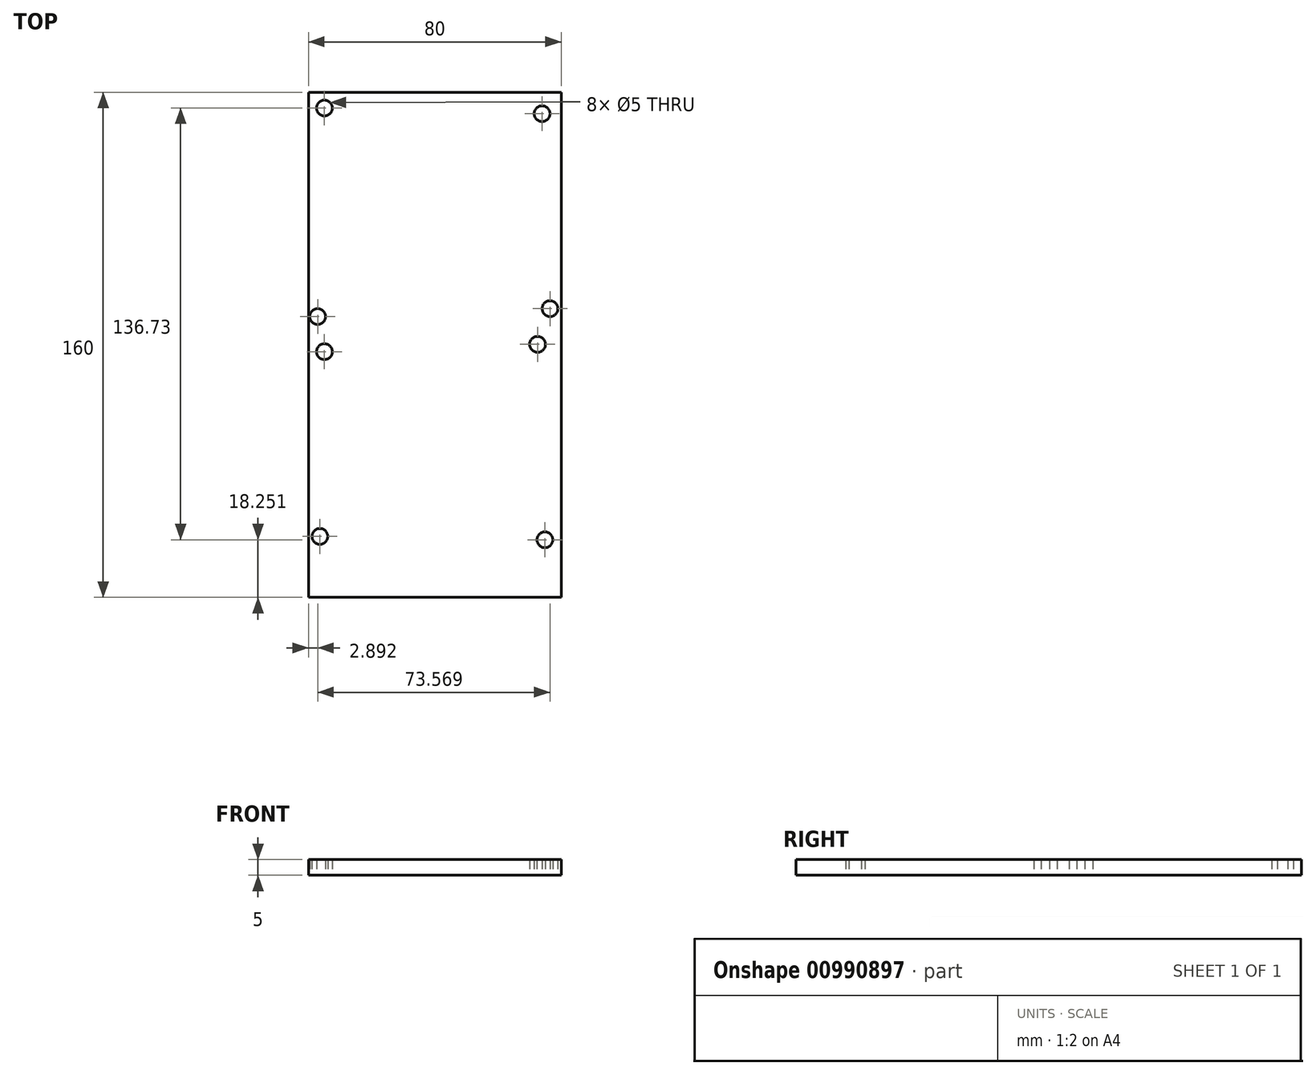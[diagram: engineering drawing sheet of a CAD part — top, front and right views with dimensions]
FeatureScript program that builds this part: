
annotation { "Feature Type Name" : "Feature", "Feature Type Description" : "" }
export const myFeature = defineFeature(function(context is Context, id is Id, definition is map)
    precondition{}
    {
        {
            var Q0;
            Q0=qCreatedBy(makeId("Top.planeOp"),FACE);
            var sketch = newSketch(context, id + "F0", { "sketchPlane" : qUnion([Q0])});
            skLineSegment(sketch, "E0.bottom", {"start": v(40, -80) * mm, "end": v(-40, -80) * mm});
            skLineSegment(sketch, "E0.top", {"start": v(40, 80) * mm, "end": v(-40, 80) * mm});
            skLineSegment(sketch, "E0.left", {"start": v(40, -80) * mm, "end": v(40, 80) * mm});
            skLineSegment(sketch, "E0.right", {"start": v(-40, -80) * mm, "end": v(-40, 80) * mm});
            skPoint(sketch, "E0.middle", {"position": v(0, 0) * mm});
            skLineSegment(sketch, "E1.bottom", {"start": v(30, -70) * mm, "end": v(-30, -70) * mm, "construction": true});
            skLineSegment(sketch, "E1.top", {"start": v(30, 70) * mm, "end": v(-30, 70) * mm, "construction": true});
            skLineSegment(sketch, "E1.left", {"start": v(30, -70) * mm, "end": v(30, 70) * mm, "construction": true});
            skLineSegment(sketch, "E1.right", {"start": v(-30, -70) * mm, "end": v(-30, 70) * mm, "construction": true});
            skCircle(sketch, "E2", {"center": v(-34.96, 74.98) * mm, "radius": 2.5 * mm});
            skCircle(sketch, "E3", {"center": v(140.96, 180.79) * mm, "radius": 2.5 * mm});
            skCircle(sketch, "E4", {"center": v(33.95, 73.2) * mm, "radius": 2.5 * mm});
            skCircle(sketch, "E5", {"center": v(36.46, 11.46) * mm, "radius": 2.5 * mm});
            skCircle(sketch, "E6", {"center": v(32.51, 0.16) * mm, "radius": 2.5 * mm});
            skCircle(sketch, "E7", {"center": v(-37.1, 8.95) * mm, "radius": 2.5 * mm});
            skCircle(sketch, "E8", {"center": v(-34.96, -2.18) * mm, "radius": 2.5 * mm});
            skCircle(sketch, "E9", {"center": v(-36.4, -60.67) * mm, "radius": 2.5 * mm});
            skCircle(sketch, "E10", {"center": v(34.85, -61.75) * mm, "radius": 2.5 * mm});
            skPoint(sketch, "E11", {"position": v(-30, 6.62) * mm});
            skPoint(sketch, "E12", {"position": v(-30, -5.4) * mm});
            skPoint(sketch, "E13", {"position": v(-30, -64.26) * mm});
            skPoint(sketch, "E14", {"position": v(30, -64.26) * mm});
            skPoint(sketch, "E15", {"position": v(30, 0) * mm});
            skPoint(sketch, "E16", {"position": v(30, 8.6) * mm});
            skPoint(sketch, "E17", {"position": v(30, -3.97) * mm});
            skPoint(sketch, "E18", {"position": v(30, 70) * mm});
            skPoint(sketch, "E19", {"position": v(-30, 70) * mm});
            skSolve(sketch);
        }
        {
            var Q0;
            Q0=makeQuery(id+"F0.imprint","IMPRINT",FACE,{"disambiguationData":[TD([[makeQuery(id+"F0.imprint","IMPRINT",EDGE,{"derivedFrom":sQuery(id+"F0.wireOp",EDGE,"E0.bottom")}),-1.0]])]});
            extrude(context, id + "F1", {"entities" : qUnion([Q0]), "depth" : 5 * mm, "offsetDistance" : 25 * mm});
        }
    });
